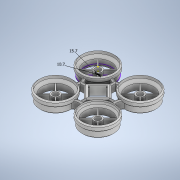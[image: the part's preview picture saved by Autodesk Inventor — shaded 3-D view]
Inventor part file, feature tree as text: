
AUTODESK INVENTOR PART (.ipt)
format: ipt  version: 2021 (Build 250183000, 183)  size: 680,960 bytes
history: native  units: in
note: dims shown in document units (in); Inventor stores cm internally (conversion verified against a paired STEP export)
features: mirror x12, sketch x8, extrude x7, chamfer x5, plane x5
ambient origin geometry x8: Origin, YZ Plane, XZ Plane, XY Plane, X Axis, Y Axis, Z Axis, Center Point
bodies: Body1 (feature_tree)
feature tree (37):
  sketch  "Sketch1"  dims[d16=0.5in d17=0.0in d18=0.189in d19=0.0787in d20=30.0deg d27=1.5748in d28=1.5748in]
  extrude  "Extrusion3"  Depth=0.189in TaperAngle=30.0deg
  chamfer  "Chamfer1"  Distance=1.5748in
  sketch  "Sketch3"  dims[d32=0.1969in d49=2.5197in d50=0.3937in d51=0.0in]
  plane  "Work Plane1"
  plane  "Work Plane2"
  mirror  "Mirror1"
  mirror  "Mirror3"
  mirror  "Mirror4"
  plane  "Work Plane6"
  extrude  "Extrusion7"  Depth=0.3937in
  chamfer  "Chamfer5"  Distance=0.3937in
  mirror  "Mirror5"
  mirror  "Mirror6"
  mirror  "Mirror7"
  extrude  "Extrusion12"  Depth=0.4213in
  mirror  "Mirror8"
  mirror  "Mirror9"
  mirror  "Mirror10"
  sketch  "Sketch17"  dims[d52=0.0787in d53=0.0787in d54=45.0deg d82=0.4213in]
  chamfer  "Chamfer9"  Distance=0.311in
  extrude  "Extrusion18"  Depth=0.3031in TaperAngle=0.0deg
  sketch  "Sketch23"  dims[d146=0.0866in d147=0.0787in d148=45.0deg d178=0.3031in d179=0.3425in d180=0.0in d181=0.0in]
  extrude  "Extrusion19"  Depth=0.1457in TaperAngle=0.0deg
  extrude  "Extrusion20"  Depth=0.0787in TaperAngle=0.0deg
  chamfer  "Chamfer11"  Distance=0.0787in Angle=45.0deg
  chamfer  "Chamfer12"  Distance=0.0787in Angle=45.0deg
  extrude  "Extrusion21"  Depth=0.0394in
  mirror  "Mirror11"
  mirror  "Mirror12"
  mirror  "Mirror13"
  plane  "Work Plane4"
  plane  "Work Plane5"
  sketch  "Sketch22"  dims[d83=0.6181in d84=0.311in d85=0.0in]
  sketch  "Sketch24"  dims[d182=0.1457in d183=0.0in d184=0.1457in d185=0.0in]
  sketch  "Sketch25"  dims[d219=0.6781in d220=0.0in d221=0.0787in d222=0.0in d223=0.0787in d224=0.0787in d225=45.0deg d226=0.0787in d227=0.0787in d228=45.0deg]
  sketch  "Sketch26"  dims[d240=0.0394in d241=0.0in d12=0.0197in d13=0.0344in d14=0.0197in d15=0.0344in d229=0.0197in d230=0.0344in d231=0.0197in d232=0.0344in]
